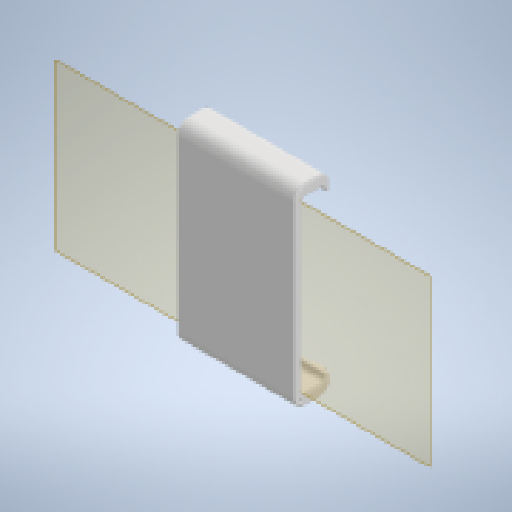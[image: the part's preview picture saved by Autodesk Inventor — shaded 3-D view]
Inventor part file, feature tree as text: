
AUTODESK INVENTOR PART (.ipt)
format: ipt  version: 2023 (Build 270158030, 158C)  size: 489,472 bytes
history: native  units: mm
features: fillet x13, extrude x5, sketch x5, reference x4, plane x2, other x2
ambient origin geometry x8: Origin, YZ Plane, XZ Plane, XY Plane, X Axis, Y Axis, Z Axis, Center Point
bodies: Solid1 (feature_tree)
feature tree (31):
  plane  "Work Plane1"
  extrude  "Extrusion1"  Depth=5.0mm
  sketch  "Sketch2"  dims[d2=50.0mm d3=25.0mm]
  plane  "Work Plane2"
  extrude  "Extrusion2"  Depth=50.0mm
  extrude  "Extrusion3"  Depth=3.0mm TaperAngle=0.0deg
  fillet  "Fillet1"  Radius=3.0mm
  fillet  "Fillet2"  Radius=3.0mm
  fillet  "Fillet3"  Radius=2.0mm
  fillet  "Fillet4"  Radius=2.0mm
  extrude  "Extrusion4"  Depth=5.0mm
  fillet  "Fillet5"  Radius=1.0mm
  fillet  "Fillet6"  Radius=2.0mm
  fillet  "Fillet7"  Radius=2.0mm
  fillet  "Fillet8"  Radius=6.0mm
  fillet  "Fillet9"  Radius=6.0mm
  fillet  "Fillet10"  Radius=0.3mm
  fillet  "Fillet11"  Radius=2.0mm
  fillet  "Fillet12"  Radius=1.0mm
  fillet  "Fillet13"  Radius=4.0mm
  extrude  "Extrusion5"  Depth=0.1mm
  sketch  "Sketch1"  dims[d0=5.0mm d1=5.0mm]
  reference  "Reference1"
  reference  "Reference2"
  reference  "Reference3"
  reference  "Reference4"
  sketch  "Sketch3"  dims[d4=3.0mm d5=0.0mm d6=3.0mm d7=0.0mm d8=3.0mm d9=3.0mm d10=2.0mm d11=0.0mm d12=2.0mm]
  sketch  "Sketch4"  dims[d13=1.0mm d14=5.0mm d15=1.0mm d16=2.0mm d17=2.0mm d18=6.0mm d19=6.0mm d20=0.3mm d21=2.0mm d22=0.0mm d23=1.0mm d24=4.0mm]
  sketch  "Sketch5"  dims[d25=0.1mm d26=0.1mm d27=1.0mm d28=1.0mm d29=1.0mm d30=0.9mm d31=0.9mm d32=1.6mm d33=2.0mm d34=1.4mm d35=2.0mm d36=0.0mm]
  other  "Assembly1"
  other  "samsung-s20:1"
